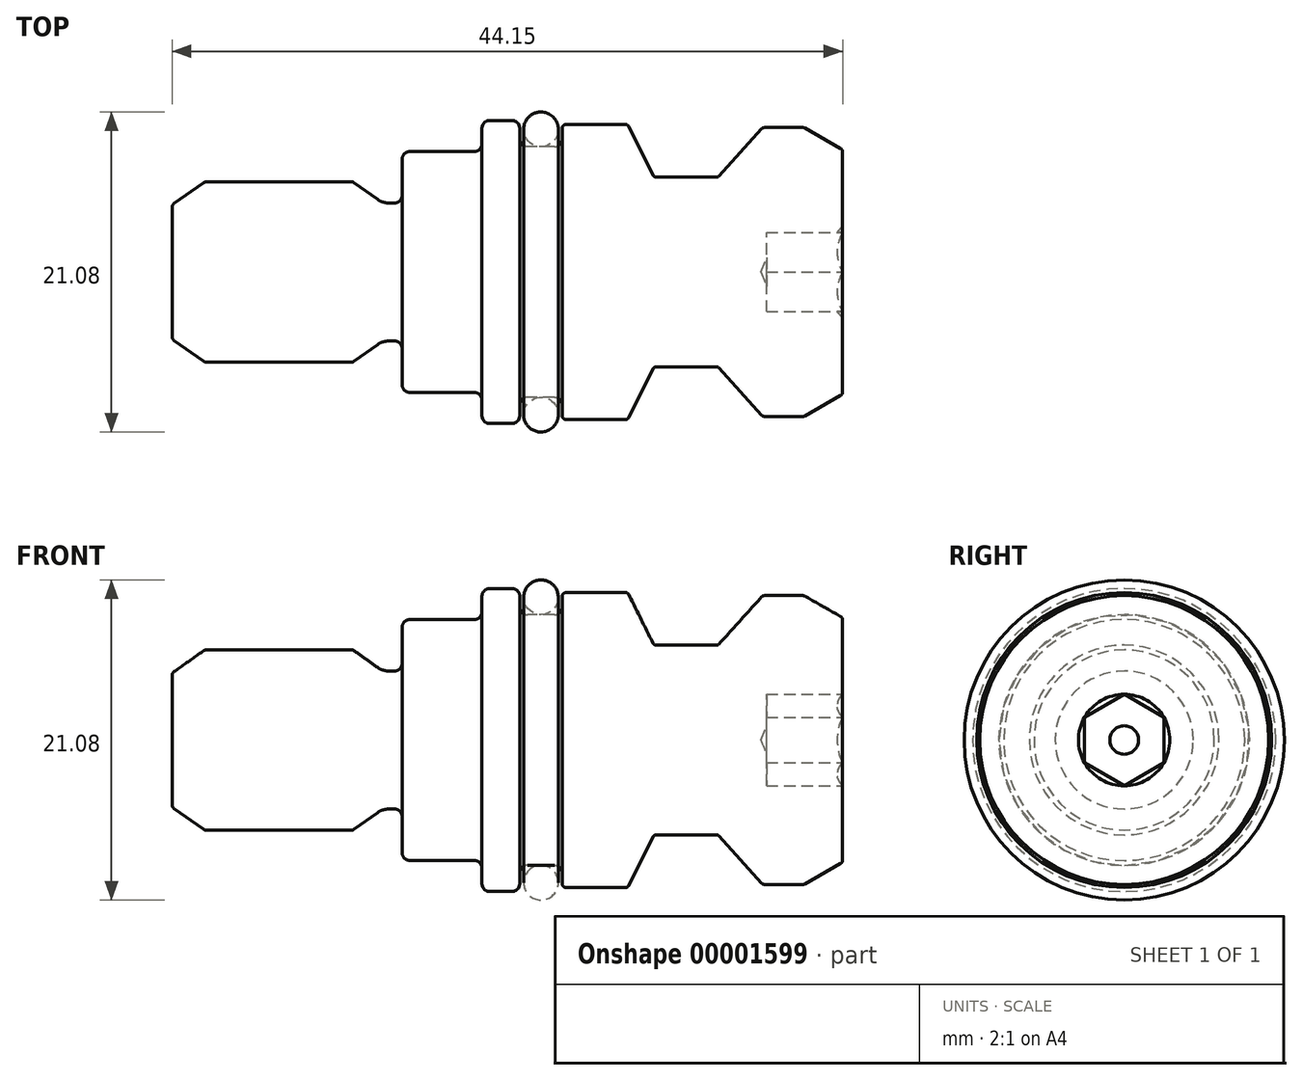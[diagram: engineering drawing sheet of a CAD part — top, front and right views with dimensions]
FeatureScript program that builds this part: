
annotation { "Feature Type Name" : "Feature", "Feature Type Description" : "" }
export const myFeature = defineFeature(function(context is Context, id is Id, definition is map)
    precondition{}
    {
        {
            var Q0;
            Q0=qCreatedBy(makeId("Front.planeOp"),FACE);
            var sketch = newSketch(context, id + "F0", { "sketchPlane" : qUnion([Q0])});
            skLineSegment(sketch, "E0", {"start": v(0, 0) * mm, "end": v(44.15, 0) * mm});
            skLineSegment(sketch, "E1", {"start": v(44.15, 0) * mm, "end": v(44.15, 7.92) * mm});
            skLineSegment(sketch, "E2", {"start": v(0, 0) * mm, "end": v(0, 4.29) * mm});
            skLineSegment(sketch, "E3", {"start": v(2.13, 0) * mm, "end": v(2.13, 5.93) * mm, "construction": true});
            skLineSegment(sketch, "E4", {"start": v(0.1, 4.5) * mm, "end": v(2.07, 5.88) * mm});
            skLineSegment(sketch, "E5", {"start": v(2.21, 5.93) * mm, "end": v(11.83, 5.93) * mm});
            skLineSegment(sketch, "E6", {"start": v(11.91, 5.93) * mm, "end": v(11.91, 0) * mm, "construction": true});
            skLineSegment(sketch, "E7", {"start": v(13.51, 0) * mm, "end": v(13.51, 4.79) * mm, "construction": true});
            skLineSegment(sketch, "E8", {"start": v(13.51, 4.79) * mm, "end": v(11.98, 5.88) * mm});
            skArc(sketch, "E9", {"start": v(13.51, 4.79) * mm, "mid": v(13.87, 4.6) * mm, "end": v(14.27, 4.54) * mm});
            skLineSegment(sketch, "E10", {"start": v(14.27, 0) * mm, "end": v(14.27, 4.54) * mm, "construction": true});
            skLineSegment(sketch, "E11", {"start": v(14.27, 4.54) * mm, "end": v(14.63, 4.54) * mm});
            skLineSegment(sketch, "E12", {"start": v(15.14, 4.54) * mm, "end": v(15.14, 0) * mm, "construction": true});
            skLineSegment(sketch, "E13", {"start": v(41.54, 9.51) * mm, "end": v(39, 9.51) * mm});
            skLineSegment(sketch, "E14", {"start": v(41.66, 9.48) * mm, "end": v(44.02, 8.14) * mm});
            skLineSegment(sketch, "E15", {"start": v(38.89, 9.51) * mm, "end": v(38.89, 0) * mm, "construction": true});
            skLineSegment(sketch, "E16", {"start": v(30.07, 9.57) * mm, "end": v(31.65, 6.39) * mm});
            skLineSegment(sketch, "E17", {"start": v(36.02, 6.33) * mm, "end": v(38.81, 9.43) * mm});
            skLineSegment(sketch, "E18", {"start": v(31.88, 6.25) * mm, "end": v(35.83, 6.25) * mm});
            skLineSegment(sketch, "E19", {"start": v(29.84, 9.72) * mm, "end": v(25.93, 9.72) * mm});
            skLineSegment(sketch, "E20", {"start": v(25.68, 9.46) * mm, "end": v(25.68, 8.76) * mm});
            skLineSegment(sketch, "E21", {"start": v(25.17, 8.26) * mm, "end": v(23.4, 8.26) * mm});
            skLineSegment(sketch, "E22", {"start": v(22.89, 8.76) * mm, "end": v(22.89, 9.47) * mm});
            skLineSegment(sketch, "E23", {"start": v(22.38, 9.98) * mm, "end": v(20.9, 9.98) * mm});
            skLineSegment(sketch, "E24", {"start": v(20.4, 9.47) * mm, "end": v(20.4, 8.45) * mm});
            skLineSegment(sketch, "E25", {"start": v(19.89, 7.94) * mm, "end": v(15.65, 7.94) * mm});
            skLineSegment(sketch, "E26", {"start": v(15.14, 7.43) * mm, "end": v(15.14, 5.05) * mm});
            skLineSegment(sketch, "E27", {"start": v(22.89, 8.26) * mm, "end": v(22.89, 0) * mm, "construction": true});
            skLineSegment(sketch, "E28", {"start": v(20.4, 7.94) * mm, "end": v(20.4, 0) * mm, "construction": true});
            skPoint(sketch, "E29.orphan", {"position": v(25.68, 0) * mm});
            skPoint(sketch, "E30.visualSharp", {"position": v(15.14, 4.54) * mm});
            skArc(sketch, "E30.filletArc", {"start": v(14.63, 4.54) * mm, "mid": v(14.99, 4.7) * mm, "end": v(15.14, 5.05) * mm});
            skPoint(sketch, "E31.visualSharp", {"position": v(15.14, 7.94) * mm});
            skArc(sketch, "E31.filletArc", {"start": v(15.65, 7.94) * mm, "mid": v(15.29, 7.79) * mm, "end": v(15.14, 7.43) * mm});
            skPoint(sketch, "E32.visualSharp", {"position": v(20.4, 7.94) * mm});
            skArc(sketch, "E32.filletArc", {"start": v(19.89, 7.94) * mm, "mid": v(20.25, 8.09) * mm, "end": v(20.4, 8.45) * mm});
            skPoint(sketch, "E33.visualSharp", {"position": v(20.4, 9.98) * mm});
            skArc(sketch, "E33.filletArc", {"start": v(20.9, 9.98) * mm, "mid": v(20.54, 9.83) * mm, "end": v(20.4, 9.47) * mm});
            skPoint(sketch, "E34.visualSharp", {"position": v(22.89, 9.98) * mm});
            skArc(sketch, "E34.filletArc", {"start": v(22.89, 9.47) * mm, "mid": v(22.74, 9.83) * mm, "end": v(22.38, 9.98) * mm});
            skPoint(sketch, "E35.visualSharp", {"position": v(22.89, 8.26) * mm});
            skArc(sketch, "E35.filletArc", {"start": v(22.89, 8.76) * mm, "mid": v(23.03, 8.4) * mm, "end": v(23.4, 8.25) * mm});
            skPoint(sketch, "E36.visualSharp", {"position": v(25.68, 8.26) * mm});
            skArc(sketch, "E36.filletArc", {"start": v(25.17, 8.26) * mm, "mid": v(25.53, 8.4) * mm, "end": v(25.68, 8.76) * mm});
            skPoint(sketch, "E37.visualSharp", {"position": v(25.68, 9.72) * mm});
            skArc(sketch, "E37.filletArc", {"start": v(25.93, 9.72) * mm, "mid": v(25.75, 9.64) * mm, "end": v(25.68, 9.46) * mm});
            skPoint(sketch, "E38.visualSharp", {"position": v(30, 9.72) * mm});
            skArc(sketch, "E38.filletArc", {"start": v(30.07, 9.57) * mm, "mid": v(29.97, 9.68) * mm, "end": v(29.84, 9.72) * mm});
            skPoint(sketch, "E39.visualSharp", {"position": v(31.72, 6.25) * mm});
            skArc(sketch, "E39.filletArc", {"start": v(31.65, 6.39) * mm, "mid": v(31.75, 6.29) * mm, "end": v(31.88, 6.25) * mm});
            skPoint(sketch, "E40.visualSharp", {"position": v(35.94, 6.25) * mm});
            skArc(sketch, "E40.filletArc", {"start": v(35.83, 6.25) * mm, "mid": v(35.93, 6.27) * mm, "end": v(36.02, 6.33) * mm});
            skPoint(sketch, "E41.visualSharp", {"position": v(38.89, 9.51) * mm});
            skArc(sketch, "E41.filletArc", {"start": v(39, 9.51) * mm, "mid": v(38.9, 9.5) * mm, "end": v(38.81, 9.43) * mm});
            skPoint(sketch, "E42.visualSharp", {"position": v(41.6, 9.51) * mm});
            skArc(sketch, "E42.filletArc", {"start": v(41.66, 9.48) * mm, "mid": v(41.6, 9.5) * mm, "end": v(41.54, 9.51) * mm});
            skPoint(sketch, "E43.visualSharp", {"position": v(44.15, 8.06) * mm});
            skArc(sketch, "E43.filletArc", {"start": v(44.15, 7.92) * mm, "mid": v(44.11, 8.04) * mm, "end": v(44.02, 8.14) * mm});
            skPoint(sketch, "E44.visualSharp", {"position": v(2.13, 5.93) * mm});
            skArc(sketch, "E44.filletArc", {"start": v(2.21, 5.93) * mm, "mid": v(2.14, 5.92) * mm, "end": v(2.07, 5.88) * mm});
            skPoint(sketch, "E45.visualSharp", {"position": v(0, 4.42) * mm});
            skArc(sketch, "E45.filletArc", {"start": v(0.1, 4.5) * mm, "mid": v(0.03, 4.4) * mm, "end": v(0, 4.29) * mm});
            skPoint(sketch, "E46.visualSharp", {"position": v(11.91, 5.93) * mm});
            skArc(sketch, "E46.filletArc", {"start": v(11.98, 5.88) * mm, "mid": v(11.9, 5.92) * mm, "end": v(11.83, 5.93) * mm});
            skLineSegment(sketch, "E47", {"start": v(44.15, 0.94) * mm, "end": v(39.14, 0.94) * mm});
            skLineSegment(sketch, "E48", {"start": v(39.14, 0.94) * mm, "end": v(38.76, 0) * mm});
            skSolve(sketch);
        }
        {
            var Q0;
            {var subQ3=sQuery(id+"F0.wireOp",EDGE,"E2");Q0=makeQuery(id+"F0.imprint","IMPRINT",FACE,{"disambiguationData":[TD([[makeQuery(id+"F0.imprint","IMPRINT",EDGE,{"derivedFrom":subQ3}),-1.0]])]});}
            var Q1;
            Q1=sQuery(id+"F0.wireOp",EDGE,"E0");
            revolve(context, id + "F1", {"entities" : qUnion([Q0]), "axis" : qUnion([Q1]), "revolveType" : RevolveType.FULL});
        }
        {
            var Q0;
            Q0=makeQuery(id+"F1.opRevolve","SWEPT_FACE",FACE,{"disambiguationData":[OSD([sQuery(id+"F0.wireOp",EDGE,"E1")])]});
            var sketch = newSketch(context, id + "F2", { "sketchPlane" : qUnion([Q0])});
            skCircle(sketch, "E49.cCircle", {"center": v(0, 0) * mm, "radius": 3 * mm, "construction": true});
            skLineSegment(sketch, "E49.0", {"start": v(0, 3) * mm, "end": v(2.6, 1.5) * mm});
            skLineSegment(sketch, "E49.1", {"start": v(2.6, 1.5) * mm, "end": v(2.6, -1.5) * mm});
            skLineSegment(sketch, "E49.2", {"start": v(2.6, -1.5) * mm, "end": v(0, -3) * mm});
            skLineSegment(sketch, "E49.3", {"start": v(0, -3) * mm, "end": v(-2.6, -1.5) * mm});
            skLineSegment(sketch, "E49.4", {"start": v(-2.6, -1.5) * mm, "end": v(-2.6, 1.5) * mm});
            skLineSegment(sketch, "E49.5", {"start": v(-2.6, 1.5) * mm, "end": v(0, 3) * mm});
            skSolve(sketch);
        }
        {
            var Q0;
            {var subQ0=makeQuery(id+"F2.imprint","IMPRINT",EDGE,{"derivedFrom":makeQuery(id+"F1.opRevolve","SWEPT_EDGE",EDGE,{"disambiguationData":[OSD([sQuery(id+"F0.wireOp",EDGE,"E1"),sQuery(id+"F0.wireOp",EDGE,"E47")])]})});Q0=qUnion([makeQuery(id+"F2.imprint","IMPRINT",FACE,{"disambiguationData":[TD([[subQ0,-1.0]])]}),makeQuery(id+"F2.imprint","IMPRINT",FACE,{"disambiguationData":[TD([[makeQuery(id+"F2.imprint","IMPRINT",EDGE,{"derivedFrom":sQuery(id+"F2.wireOp",EDGE,"E49.0")}),-1.0]])]})]);}
            extrude(context, id + "F3", {"entities" : qUnion([Q0]), "operationType" : NewBodyOperationType.REMOVE, "oppositeDirection" : true, "depth" : 5 * mm});
        }
        {
            var Q0;
            Q0=qCreatedBy(makeId("Front.planeOp"),FACE);
            var sketch = newSketch(context, id + "F4", { "sketchPlane" : qUnion([Q0])});
            skPoint(sketch, "E50.0", {"position": v(44.15, 3) * mm});
            skPoint(sketch, "E50.1", {"position": v(44.15, -3) * mm});
            skArc(sketch, "E51", {"start": v(44.15, 3) * mm, "mid": v(42.88, 0) * mm, "end": v(44.15, -3) * mm});
            skLineSegment(sketch, "E52", {"start": v(44.15, -3) * mm, "end": v(44.15, 0) * mm});
            skLineSegment(sketch, "E53", {"start": v(44.15, 0) * mm, "end": v(42.88, 0) * mm});
            skSolve(sketch);
        }
        {
            var Q0;
            {var subQ1=sQuery(id+"F4.wireOp",EDGE,"E52");Q0=makeQuery(id+"F4.imprint","IMPRINT",FACE,{"disambiguationData":[TD([[makeQuery(id+"F4.imprint","IMPRINT",EDGE,{"derivedFrom":subQ1}),1.0]])]});}
            var Q1;
            Q1=sQuery(id+"F4.wireOp",EDGE,"E53");
            revolve(context, id + "F5", {"operationType" : NewBodyOperationType.REMOVE, "entities" : qUnion([Q0]), "axis" : qUnion([Q1]), "revolveType" : RevolveType.FULL, "oppositeDirection" : true});
        }
        {
            var Q0;
            Q0=qCreatedBy(makeId("Front.planeOp"),FACE);
            var sketch = newSketch(context, id + "F6", { "sketchPlane" : qUnion([Q0])});
            skCircle(sketch, "E54", {"center": v(24.28, 9.4) * mm, "radius": 1.14 * mm});
            skLineSegment(sketch, "E55.0", {"start": v(23.4, -8.25) * mm, "end": v(23.4, 8.25) * mm, "construction": true});
            skLineSegment(sketch, "E55.1", {"start": v(25.17, -8.26) * mm, "end": v(25.17, 8.26) * mm, "construction": true});
            skLineSegment(sketch, "E56", {"start": v(25.17, 0) * mm, "end": v(23.4, 0) * mm, "construction": true});
            skLineSegment(sketch, "E57", {"start": v(24.28, 0) * mm, "end": v(24.28, 8.25) * mm, "construction": true});
            skLineSegment(sketch, "E58", {"start": v(25.17, 8.25) * mm, "end": v(23.4, 8.25) * mm});
            skSolve(sketch);
        }
        {
            var Q0;
            Q0=makeQuery(id+"F6.imprint","IMPRINT",FACE,{"disambiguationData":[TD([[makeQuery(id+"F6.imprint","IMPRINT",EDGE,{"derivedFrom":sQuery(id+"F6.wireOp",EDGE,"E54")}),1.0]])]});
            var Q1;
            Q1=sQuery(id+"F6.wireOp",EDGE,"E56");
            revolve(context, id + "F7", {"entities" : qUnion([Q0]), "axis" : qUnion([Q1]), "revolveType" : RevolveType.FULL});
        }
    });
